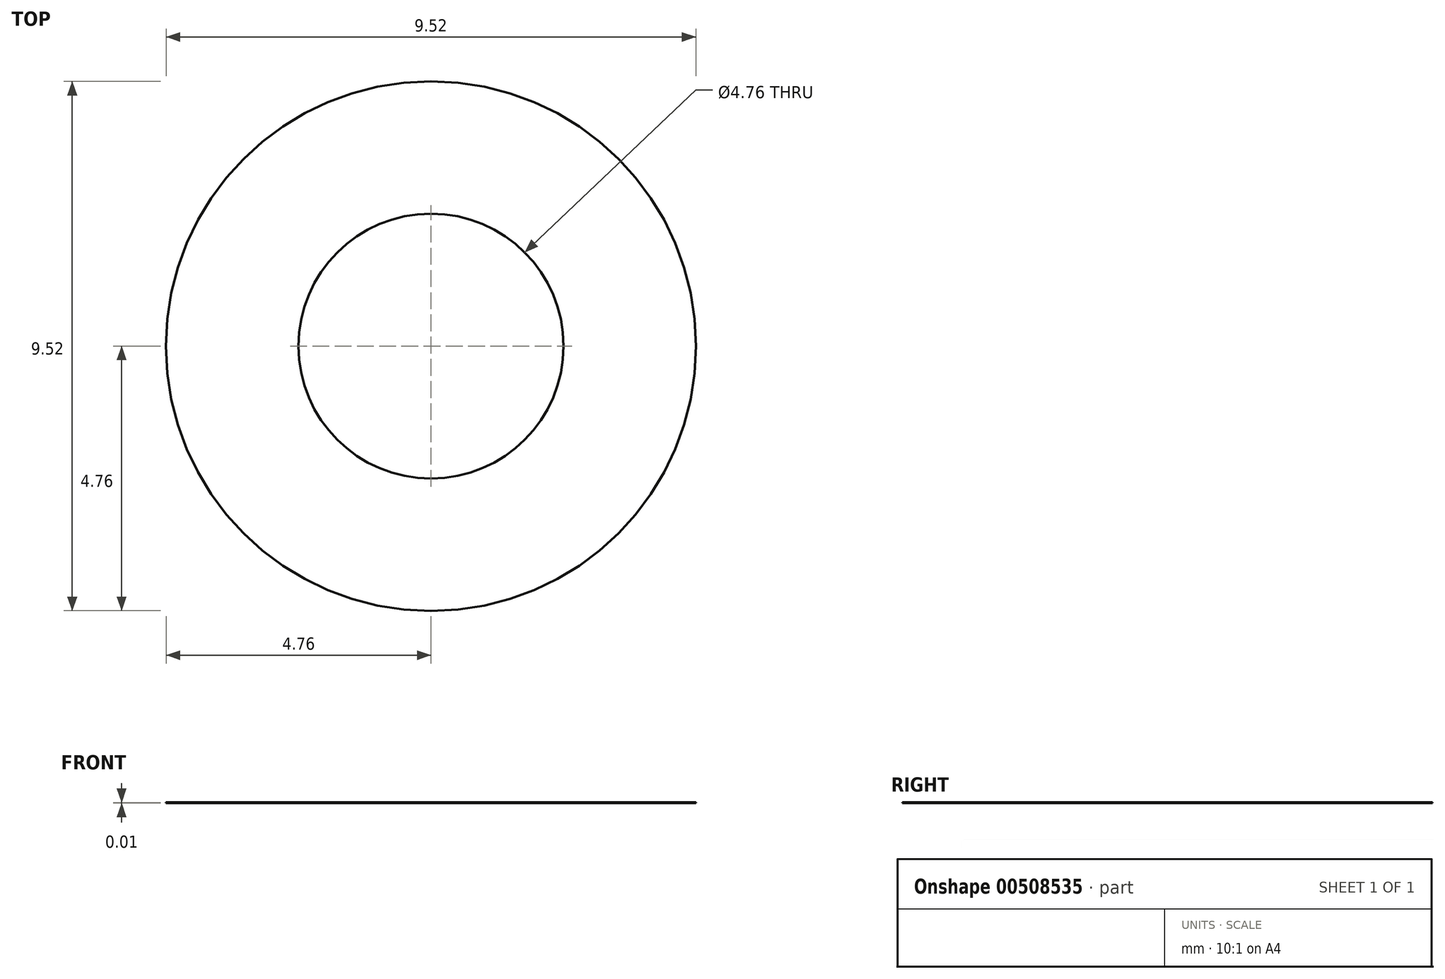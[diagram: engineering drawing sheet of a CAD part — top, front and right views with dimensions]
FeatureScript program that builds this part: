
annotation { "Feature Type Name" : "Feature", "Feature Type Description" : "" }
export const myFeature = defineFeature(function(context is Context, id is Id, definition is map)
    precondition{}
    {
        {
            var Q0;
            Q0=qCreatedBy(makeId("Top.planeOp"),FACE);
            var sketch = newSketch(context, id + "F0", { "sketchPlane" : qUnion([Q0])});
            skCircle(sketch, "E0", {"center": v(0, 0) * mm, "radius": 4.76 * mm});
            skCircle(sketch, "E1", {"center": v(0, 0) * mm, "radius": 2.38 * mm});
            skSolve(sketch);
        }
        {
            var Q0;
            Q0 = qSketchRegion(id + "F0", true);
            extrude(context, id + "F1", {"entities" : qUnion([Q0]), "depth" : 3 / 203.2 * mm});
        }
    });
